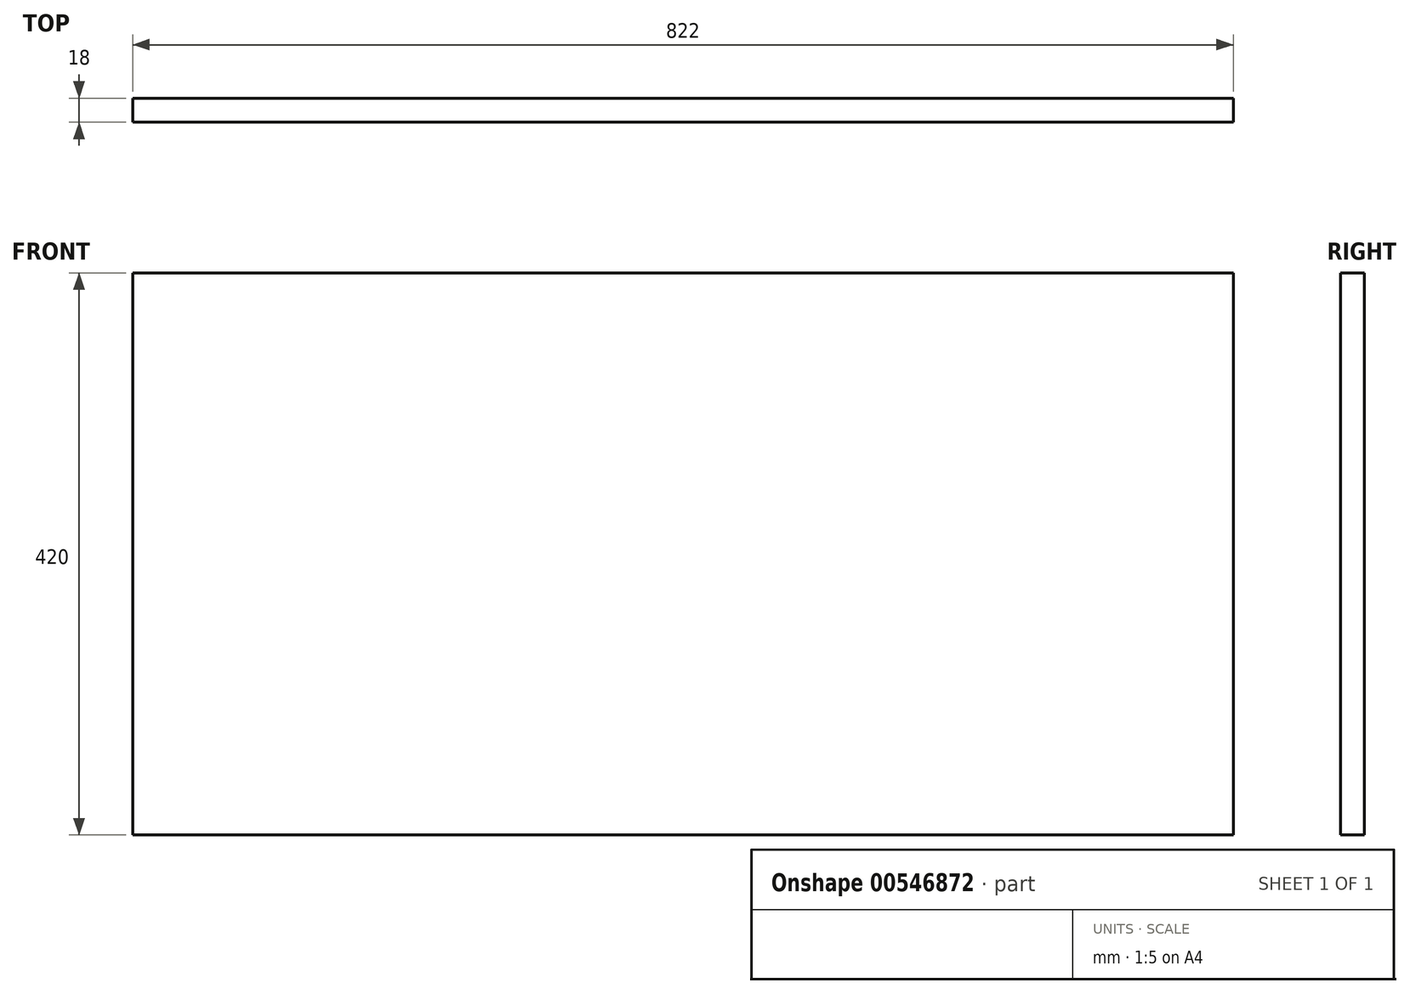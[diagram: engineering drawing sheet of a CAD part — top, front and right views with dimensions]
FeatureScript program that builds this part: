
annotation { "Feature Type Name" : "Feature", "Feature Type Description" : "" }
export const myFeature = defineFeature(function(context is Context, id is Id, definition is map)
    precondition{}
    {
        {
            var Q0;
            Q0=qCreatedBy(makeId("Front.planeOp"),FACE);
            var sketch = newSketch(context, id + "F0", { "sketchPlane" : qUnion([Q0])});
            skLineSegment(sketch, "E0.bottom", {"start": v(-387.21, -223.6) * mm, "end": v(434.79, -223.6) * mm});
            skLineSegment(sketch, "E0.top", {"start": v(-387.21, 196.4) * mm, "end": v(434.79, 196.4) * mm});
            skLineSegment(sketch, "E0.left", {"start": v(-387.21, -223.6) * mm, "end": v(-387.21, 196.4) * mm});
            skLineSegment(sketch, "E0.right", {"start": v(434.79, -223.6) * mm, "end": v(434.79, 196.4) * mm});
            skSolve(sketch);
        }
        {
            var Q0;
            Q0 = qSketchRegion(id + "F0", true);
            extrude(context, id + "F1", {"entities" : qUnion([Q0]), "depth" : 18 * mm, "offsetDistance" : 25 * mm});
        }
    });
